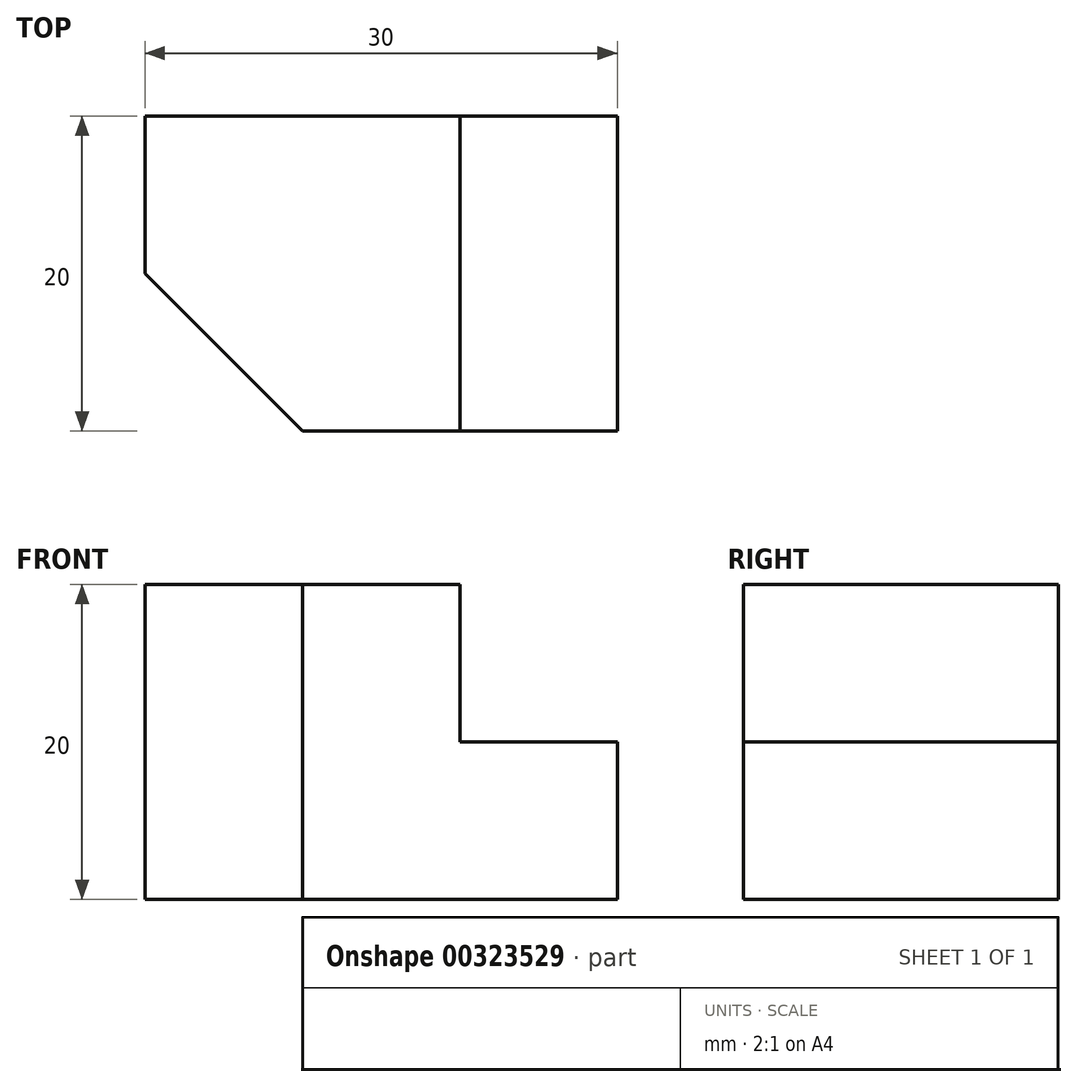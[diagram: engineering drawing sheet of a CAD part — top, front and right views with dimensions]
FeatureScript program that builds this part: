
annotation { "Feature Type Name" : "Feature", "Feature Type Description" : "" }
export const myFeature = defineFeature(function(context is Context, id is Id, definition is map)
    precondition{}
    {
        {
            var Q0;
            Q0=qCreatedBy(makeId("Front.planeOp"),FACE);
            var sketch = newSketch(context, id + "F0", { "sketchPlane" : qUnion([Q0])});
            skLineSegment(sketch, "E0.bottom", {"start": v(0, 0) * mm, "end": v(30, 0) * mm});
            skLineSegment(sketch, "E0.top", {"start": v(0, 20) * mm, "end": v(30, 20) * mm});
            skLineSegment(sketch, "E0.left", {"start": v(0, 0) * mm, "end": v(0, 20) * mm});
            skLineSegment(sketch, "E0.right", {"start": v(30, 0) * mm, "end": v(30, 20) * mm});
            skSolve(sketch);
        }
        {
            var Q0;
            Q0 = qSketchRegion(id + "F0", true);
            extrude(context, id + "F1", {"entities" : qUnion([Q0]), "oppositeDirection" : true, "depth" : 20 * mm});
        }
        {
            var Q0;
            Q0=makeQuery(id+"F1.opExtrude","SWEPT_FACE",FACE,{"disambiguationData":[OSD([sQuery(id+"F0.wireOp",EDGE,"E0.top")])]});
            var sketch = newSketch(context, id + "F2", { "sketchPlane" : qUnion([Q0])});
            skLineSegment(sketch, "E1", {"start": v(0, 0) * mm, "end": v(10, 0) * mm});
            skLineSegment(sketch, "E2", {"start": v(10, 0) * mm, "end": v(0, 10) * mm});
            skLineSegment(sketch, "E3", {"start": v(0, 10) * mm, "end": v(0, 0) * mm});
            skSolve(sketch);
        }
        {
            var Q0;
            Q0 = qSketchRegion(id + "F2", true);
            extrude(context, id + "F3", {"entities" : qUnion([Q0]), "operationType" : NewBodyOperationType.REMOVE, "oppositeDirection" : true, "depth" : 25 * mm});
        }
        {
            var Q0;
            Q0=makeQuery(id+"F1.opExtrude","CAP_FACE",FACE,{"disambiguationData":[OSD([sQuery(id+"F0.wireOp",EDGE,"E0.bottom"),sQuery(id+"F0.wireOp",EDGE,"E0.top"),sQuery(id+"F0.wireOp",EDGE,"E0.left"),sQuery(id+"F0.wireOp",EDGE,"E0.right")])],"isStart":true});
            var sketch = newSketch(context, id + "F4", { "sketchPlane" : qUnion([Q0])});
            skPoint(sketch, "E4.oppositeSnap0", {"position": v(20, 20) * mm});
            skLineSegment(sketch, "E4.bottom", {"start": v(30, 20) * mm, "end": v(20, 20) * mm});
            skLineSegment(sketch, "E4.top", {"start": v(30, 10) * mm, "end": v(20, 10) * mm});
            skLineSegment(sketch, "E4.left", {"start": v(30, 20) * mm, "end": v(30, 10) * mm});
            skLineSegment(sketch, "E4.right", {"start": v(20, 20) * mm, "end": v(20, 10) * mm});
            skSolve(sketch);
        }
        {
            var Q0;
            Q0 = qSketchRegion(id + "F4", true);
            extrude(context, id + "F5", {"entities" : qUnion([Q0]), "operationType" : NewBodyOperationType.REMOVE, "oppositeDirection" : true, "depth" : 25 * mm});
        }
    });
